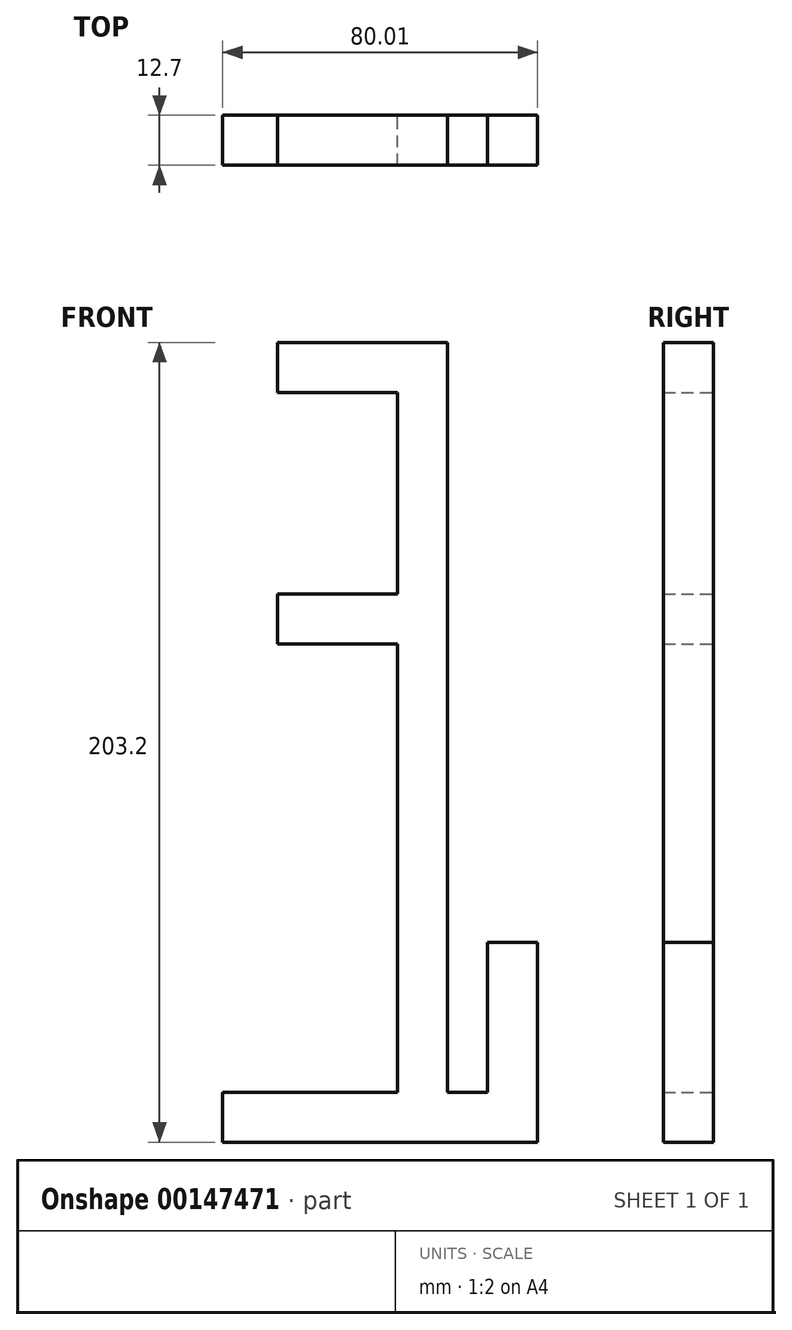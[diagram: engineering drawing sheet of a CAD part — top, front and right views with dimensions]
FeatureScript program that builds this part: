
annotation { "Feature Type Name" : "Feature", "Feature Type Description" : "" }
export const myFeature = defineFeature(function(context is Context, id is Id, definition is map)
    precondition{}
    {
        {
            var Q0;
            Q0=qCreatedBy(makeId("Front.planeOp"),FACE);
            var sketch = newSketch(context, id + "F0", { "sketchPlane" : qUnion([Q0])});
            skLineSegment(sketch, "E0.bottom", {"start": v(6.35, -101.6) * mm, "end": v(-6.35, -101.6) * mm});
            skLineSegment(sketch, "E0.top", {"start": v(6.35, 101.6) * mm, "end": v(-6.35, 101.6) * mm});
            skLineSegment(sketch, "E0.left", {"start": v(6.35, -101.6) * mm, "end": v(6.35, 101.6) * mm});
            skLineSegment(sketch, "E0.right", {"start": v(-6.35, -101.6) * mm, "end": v(-6.35, 101.6) * mm});
            skPoint(sketch, "E0.middle", {"position": v(0, 0) * mm});
            skLineSegment(sketch, "E1.bottom", {"start": v(6.35, 101.6) * mm, "end": v(-36.83, 101.6) * mm});
            skLineSegment(sketch, "E1.top", {"start": v(6.35, 88.9) * mm, "end": v(-36.83, 88.9) * mm});
            skLineSegment(sketch, "E1.left", {"start": v(6.35, 101.6) * mm, "end": v(6.35, 88.9) * mm});
            skLineSegment(sketch, "E1.right", {"start": v(-36.83, 101.6) * mm, "end": v(-36.83, 88.9) * mm});
            skLineSegment(sketch, "E2.bottom", {"start": v(6.35, 37.72) * mm, "end": v(-36.83, 37.72) * mm});
            skLineSegment(sketch, "E2.top", {"start": v(6.35, 25.02) * mm, "end": v(-36.83, 25.02) * mm});
            skLineSegment(sketch, "E2.left", {"start": v(6.35, 37.72) * mm, "end": v(6.35, 25.02) * mm});
            skLineSegment(sketch, "E2.right", {"start": v(-36.83, 37.72) * mm, "end": v(-36.83, 25.02) * mm});
            skLineSegment(sketch, "E3.bottom", {"start": v(6.35, -101.6) * mm, "end": v(29.21, -101.6) * mm});
            skLineSegment(sketch, "E3.top", {"start": v(6.35, -88.9) * mm, "end": v(29.21, -88.9) * mm});
            skLineSegment(sketch, "E3.left", {"start": v(6.35, -101.6) * mm, "end": v(6.35, -88.9) * mm});
            skLineSegment(sketch, "E3.right", {"start": v(29.2, -101.6) * mm, "end": v(29.2, -88.9) * mm});
            skLineSegment(sketch, "E4.bottom", {"start": v(29.21, -88.9) * mm, "end": v(16.51, -88.9) * mm});
            skLineSegment(sketch, "E4.top", {"start": v(29.21, -50.8) * mm, "end": v(16.51, -50.8) * mm});
            skLineSegment(sketch, "E4.left", {"start": v(29.2, -88.9) * mm, "end": v(29.2, -50.8) * mm});
            skLineSegment(sketch, "E4.right", {"start": v(16.5, -88.9) * mm, "end": v(16.5, -50.8) * mm});
            skLineSegment(sketch, "E5.bottom", {"start": v(-6.35, -101.6) * mm, "end": v(-50.8, -101.6) * mm});
            skLineSegment(sketch, "E5.top", {"start": v(-6.35, -88.9) * mm, "end": v(-50.8, -88.9) * mm});
            skLineSegment(sketch, "E5.left", {"start": v(-6.35, -101.6) * mm, "end": v(-6.35, -88.9) * mm});
            skLineSegment(sketch, "E5.right", {"start": v(-50.8, -101.6) * mm, "end": v(-50.8, -88.9) * mm});
            skSolve(sketch);
        }
        {
            var Q0;
            Q0 = qSketchRegion(id + "F0", true);
            var Q1;
            {var subQ5=sQuery(id+"F0.wireOp",EDGE,"E1.right");Q1=makeQuery(id+"F0.imprint","IMPRINT",FACE,{"disambiguationData":[TD([[makeQuery(id+"F0.imprint","IMPRINT",EDGE,{"derivedFrom":subQ5}),1.0]])]});}
            extrude(context, id + "F1", {"entities" : qUnion([Q0, Q1]), "endBound" : BoundingType.SYMMETRIC, "depth" : 12.7 * mm});
        }
    });
